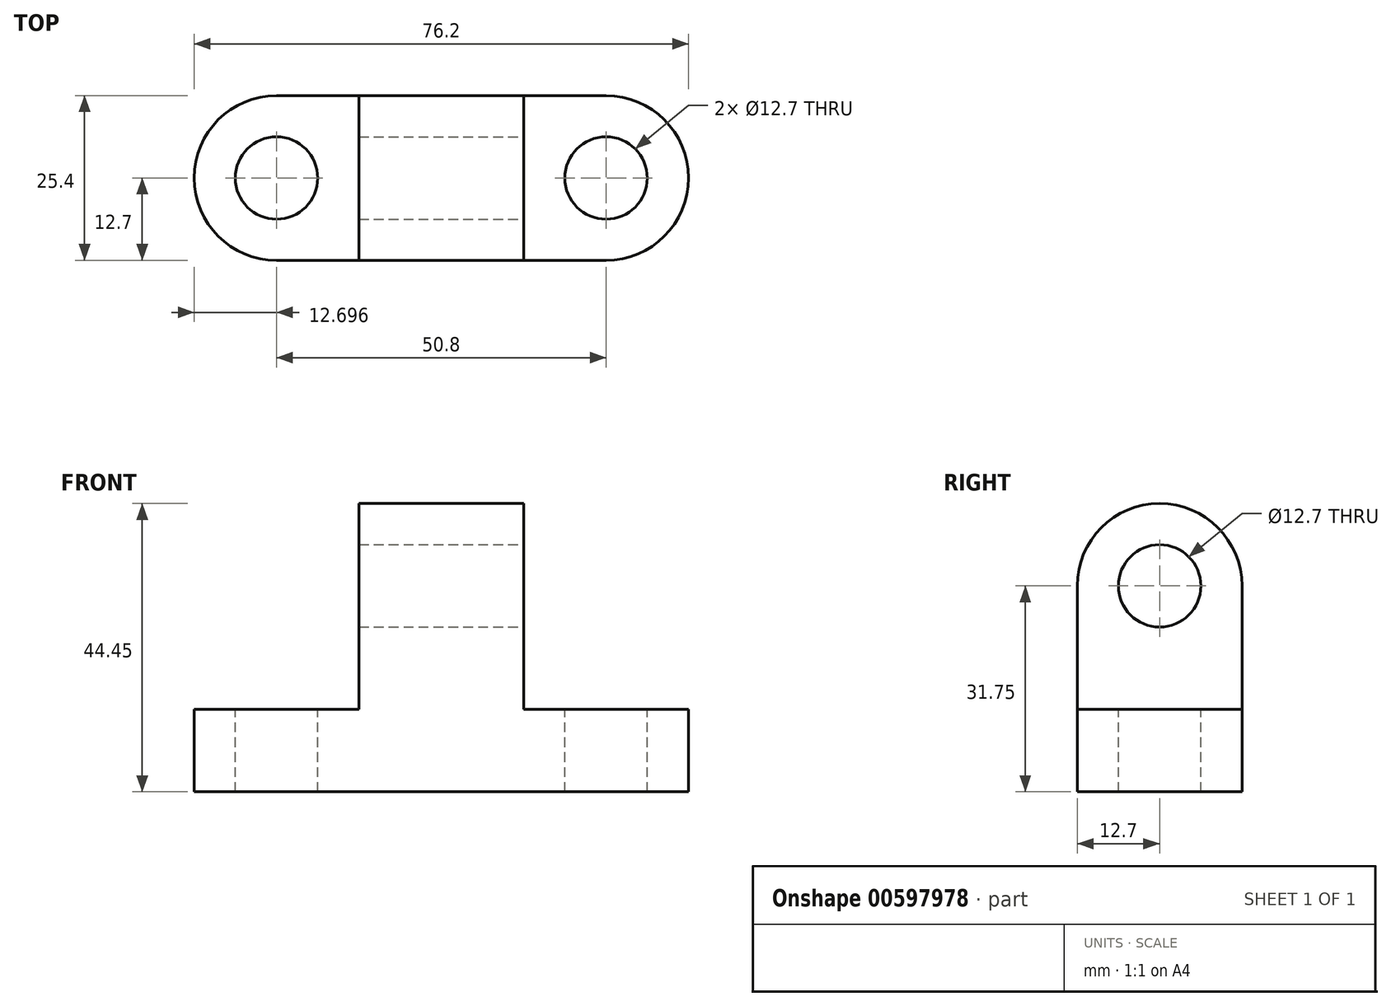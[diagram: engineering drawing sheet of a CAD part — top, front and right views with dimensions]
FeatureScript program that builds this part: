
annotation { "Feature Type Name" : "Feature", "Feature Type Description" : "" }
export const myFeature = defineFeature(function(context is Context, id is Id, definition is map)
    precondition{}
    {
        {
            var Q0;
            Q0=qCreatedBy(makeId("Front.planeOp"),FACE);
            var sketch = newSketch(context, id + "F0", { "sketchPlane" : qUnion([Q0])});
            skLineSegment(sketch, "E0", {"start": v(-73.05, 0) * mm, "end": v(3.15, 0) * mm});
            skLineSegment(sketch, "E1", {"start": v(3.15, 0) * mm, "end": v(3.15, 12.7) * mm});
            skLineSegment(sketch, "E2", {"start": v(3.15, 12.7) * mm, "end": v(-22.25, 12.7) * mm});
            skLineSegment(sketch, "E3", {"start": v(-22.25, 12.7) * mm, "end": v(-22.25, 44.45) * mm});
            skLineSegment(sketch, "E4", {"start": v(-22.25, 44.45) * mm, "end": v(-47.65, 44.45) * mm});
            skLineSegment(sketch, "E5", {"start": v(-47.65, 44.45) * mm, "end": v(-47.65, 12.7) * mm});
            skLineSegment(sketch, "E6", {"start": v(-47.65, 12.7) * mm, "end": v(-73.05, 12.7) * mm});
            skLineSegment(sketch, "E7", {"start": v(-73.05, 12.7) * mm, "end": v(-73.05, 0) * mm});
            skSolve(sketch);
        }
        {
            var Q0;
            Q0=makeQuery(id+"F0.imprint","IMPRINT",FACE,{"disambiguationData":[TD([[makeQuery(id+"F0.imprint","IMPRINT",EDGE,{"derivedFrom":sQuery(id+"F0.wireOp",EDGE,"E0")}),1.0]])]});
            extrude(context, id + "F1", {"entities" : qUnion([Q0]), "depth" : 25.4 * mm, "offsetDistance" : 25.4 * mm});
        }
        {
            var Q0;
            Q0=makeQuery(id+"F1.opExtrude","SWEPT_FACE",FACE,{"disambiguationData":[OSD([sQuery(id+"F0.wireOp",EDGE,"E2")])]});
            var sketch = newSketch(context, id + "F2", { "sketchPlane" : qUnion([Q0])});
            skArc(sketch, "E8", {"start": v(-9.55, -25.4) * mm, "mid": v(3.15, -12.7) * mm, "end": v(-9.55, 0) * mm});
            skSolve(sketch);
        }
        {
            var Q0;
            Q0=makeQuery(id+"F1.opExtrude","SWEPT_FACE",FACE,{"disambiguationData":[OSD([sQuery(id+"F0.wireOp",EDGE,"E6")])]});
            var sketch = newSketch(context, id + "F3", { "sketchPlane" : qUnion([Q0])});
            skArc(sketch, "E9", {"start": v(-60.35, 0) * mm, "mid": v(-73.05, -12.7) * mm, "end": v(-60.35, -25.4) * mm});
            skSolve(sketch);
        }
        {
            var Q0;
            {var subQ0=sQuery(id+"F3.wireOp",EDGE,"E9");var subQ1=sQuery(id+"F0.wireOp",EDGE,"E6");var subQ2=makeQuery(id+"F1.opExtrude","CAP_EDGE",EDGE,{"disambiguationData":[OSD([subQ1])],"isStart":true});var subQ3=makeQuery(id+"F3.imprint","INTERSECT",VERTEX,{"derivedFrom":[subQ2,subQ0]});Q0=makeQuery(id+"F3.imprint","IMPRINT",FACE,{"disambiguationData":[TD([[makeQuery(id+"F3.imprint","IMPRINT",EDGE,{"disambiguationData":[TD([[subQ3,-1.0]])],"derivedFrom":subQ0}),-1.0]])]});}
            var Q1;
            {var subQ0=sQuery(id+"F3.wireOp",EDGE,"E9");var subQ1=sQuery(id+"F0.wireOp",EDGE,"E6");var subQ2=makeQuery(id+"F1.opExtrude","CAP_EDGE",EDGE,{"disambiguationData":[OSD([subQ1])],"isStart":false});var subQ3=makeQuery(id+"F3.imprint","INTERSECT",VERTEX,{"derivedFrom":[subQ2,subQ0]});Q1=makeQuery(id+"F3.imprint","IMPRINT",FACE,{"disambiguationData":[TD([[makeQuery(id+"F3.imprint","IMPRINT",EDGE,{"disambiguationData":[TD([[subQ3,1.0]])],"derivedFrom":subQ0}),-1.0]])]});}
            var Q2;
            {var subQ0=sQuery(id+"F2.wireOp",EDGE,"E8");var subQ1=sQuery(id+"F0.wireOp",EDGE,"E2");var subQ2=makeQuery(id+"F1.opExtrude","CAP_EDGE",EDGE,{"disambiguationData":[OSD([subQ1])],"isStart":true});var subQ3=makeQuery(id+"F2.imprint","INTERSECT",VERTEX,{"derivedFrom":[subQ2,subQ0]});Q2=makeQuery(id+"F2.imprint","IMPRINT",FACE,{"disambiguationData":[TD([[makeQuery(id+"F2.imprint","IMPRINT",EDGE,{"disambiguationData":[TD([[subQ3,1.0]])],"derivedFrom":subQ0}),-1.0]])]});}
            var Q3;
            {var subQ0=sQuery(id+"F2.wireOp",EDGE,"E8");var subQ1=sQuery(id+"F0.wireOp",EDGE,"E2");var subQ2=makeQuery(id+"F1.opExtrude","CAP_EDGE",EDGE,{"disambiguationData":[OSD([subQ1])],"isStart":false});var subQ3=makeQuery(id+"F2.imprint","INTERSECT",VERTEX,{"derivedFrom":[subQ2,subQ0]});Q3=makeQuery(id+"F2.imprint","IMPRINT",FACE,{"disambiguationData":[TD([[makeQuery(id+"F2.imprint","IMPRINT",EDGE,{"disambiguationData":[TD([[subQ3,-1.0]])],"derivedFrom":subQ0}),-1.0]])]});}
            extrude(context, id + "F4", {"entities" : qUnion([Q0, Q1, Q2, Q3]), "operationType" : NewBodyOperationType.REMOVE, "oppositeDirection" : true, "depth" : 25.4 * mm, "offsetDistance" : 25.4 * mm});
        }
        {
            var Q0;
            Q0=makeQuery(id+"F1.opExtrude","SWEPT_FACE",FACE,{"disambiguationData":[OSD([sQuery(id+"F0.wireOp",EDGE,"E2")])]});
            var sketch = newSketch(context, id + "F5", { "sketchPlane" : qUnion([Q0])});
            skCircle(sketch, "E10", {"center": v(-9.55, -12.7) * mm, "radius": 6.35 * mm});
            skSolve(sketch);
        }
        {
            var Q0;
            Q0=makeQuery(id+"F1.opExtrude","SWEPT_FACE",FACE,{"disambiguationData":[OSD([sQuery(id+"F0.wireOp",EDGE,"E6")])]});
            var sketch = newSketch(context, id + "F6", { "sketchPlane" : qUnion([Q0])});
            skCircle(sketch, "E11", {"center": v(-60.35, -12.7) * mm, "radius": 6.35 * mm});
            skSolve(sketch);
        }
        {
            var Q0;
            Q0=makeQuery(id+"F6.imprint","IMPRINT",FACE,{"disambiguationData":[TD([[makeQuery(id+"F6.imprint","IMPRINT",EDGE,{"derivedFrom":sQuery(id+"F6.wireOp",EDGE,"E11")}),1.0]])]});
            var Q1;
            Q1=makeQuery(id+"F5.imprint","IMPRINT",FACE,{"disambiguationData":[TD([[makeQuery(id+"F5.imprint","IMPRINT",EDGE,{"derivedFrom":sQuery(id+"F5.wireOp",EDGE,"E10")}),1.0]])]});
            extrude(context, id + "F7", {"entities" : qUnion([Q0, Q1]), "operationType" : NewBodyOperationType.REMOVE, "oppositeDirection" : true, "depth" : 25.4 * mm, "offsetDistance" : 25.4 * mm});
        }
        {
            var Q0;
            Q0=makeQuery(id+"F1.opExtrude","SWEPT_FACE",FACE,{"disambiguationData":[OSD([sQuery(id+"F0.wireOp",EDGE,"E3")])]});
            var sketch = newSketch(context, id + "F8", { "sketchPlane" : qUnion([Q0])});
            skArc(sketch, "E12", {"start": v(0, 31.75) * mm, "mid": v(-12.7, 44.45) * mm, "end": v(-25.4, 31.75) * mm});
            skSolve(sketch);
        }
        {
            var Q0;
            {var subQ0=sQuery(id+"F8.wireOp",EDGE,"E12");var subQ1=sQuery(id+"F0.wireOp",EDGE,"E3");var subQ2=makeQuery(id+"F1.opExtrude","CAP_EDGE",EDGE,{"disambiguationData":[OSD([subQ1])],"isStart":false});var subQ3=makeQuery(id+"F8.imprint","INTERSECT",VERTEX,{"derivedFrom":[subQ2,subQ0]});Q0=makeQuery(id+"F8.imprint","IMPRINT",FACE,{"disambiguationData":[TD([[makeQuery(id+"F8.imprint","IMPRINT",EDGE,{"disambiguationData":[TD([[subQ3,1.0]])],"derivedFrom":subQ0}),-1.0]])]});}
            var Q1;
            {var subQ0=sQuery(id+"F8.wireOp",EDGE,"E12");var subQ1=sQuery(id+"F0.wireOp",EDGE,"E3");var subQ2=makeQuery(id+"F1.opExtrude","CAP_EDGE",EDGE,{"disambiguationData":[OSD([subQ1])],"isStart":true});var subQ3=makeQuery(id+"F8.imprint","INTERSECT",VERTEX,{"derivedFrom":[subQ2,subQ0]});Q1=makeQuery(id+"F8.imprint","IMPRINT",FACE,{"disambiguationData":[TD([[makeQuery(id+"F8.imprint","IMPRINT",EDGE,{"disambiguationData":[TD([[subQ3,-1.0]])],"derivedFrom":subQ0}),-1.0]])]});}
            extrude(context, id + "F9", {"entities" : qUnion([Q0, Q1]), "operationType" : NewBodyOperationType.REMOVE, "oppositeDirection" : true, "depth" : 25.4 * mm, "offsetDistance" : 25.4 * mm});
        }
        {
            var Q0;
            Q0=makeQuery(id+"F1.opExtrude","SWEPT_FACE",FACE,{"disambiguationData":[OSD([sQuery(id+"F0.wireOp",EDGE,"E3")])]});
            var sketch = newSketch(context, id + "F10", { "sketchPlane" : qUnion([Q0])});
            skCircle(sketch, "E13", {"center": v(-12.7, 31.75) * mm, "radius": 6.35 * mm});
            skSolve(sketch);
        }
        {
            var Q0;
            Q0=makeQuery(id+"F10.imprint","IMPRINT",FACE,{"disambiguationData":[TD([[makeQuery(id+"F10.imprint","IMPRINT",EDGE,{"derivedFrom":sQuery(id+"F10.wireOp",EDGE,"E13")}),1.0]])]});
            extrude(context, id + "F11", {"entities" : qUnion([Q0]), "operationType" : NewBodyOperationType.REMOVE, "oppositeDirection" : true, "depth" : 25.4 * mm, "offsetDistance" : 25.4 * mm});
        }
    });
